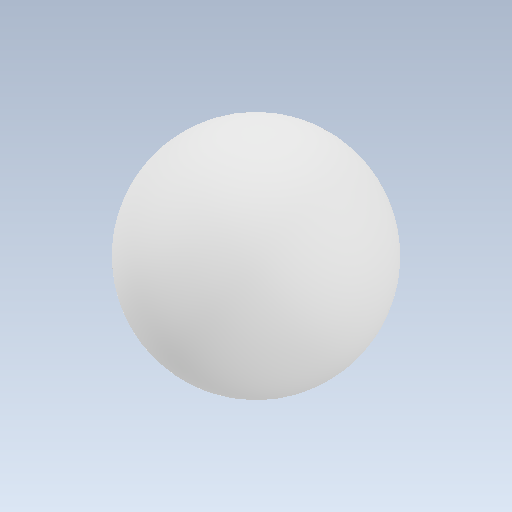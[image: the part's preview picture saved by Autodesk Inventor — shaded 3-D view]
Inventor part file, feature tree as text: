
AUTODESK INVENTOR PART (.ipt)
format: ipt  version: 2020 (Build 240168000, 168)  size: 117,760 bytes
history: native  units: in
note: dims shown in document units (in); Inventor stores cm internally (conversion verified against a paired STEP export)
features: revolve x1
ambient origin geometry x8: Origin, YZ Plane, XZ Plane, XY Plane, X Axis, Y Axis, Z Axis, Center Point
bodies: Solid1 (feature_tree)
feature tree (1):
  revolve  "Revolve1"  [1 undecoded]
note: 1 required parameter value undecoded (feature->parameter linkage not recoverable at this tier; creation-order binding heuristic only, values carry confidence <= 0.55)
